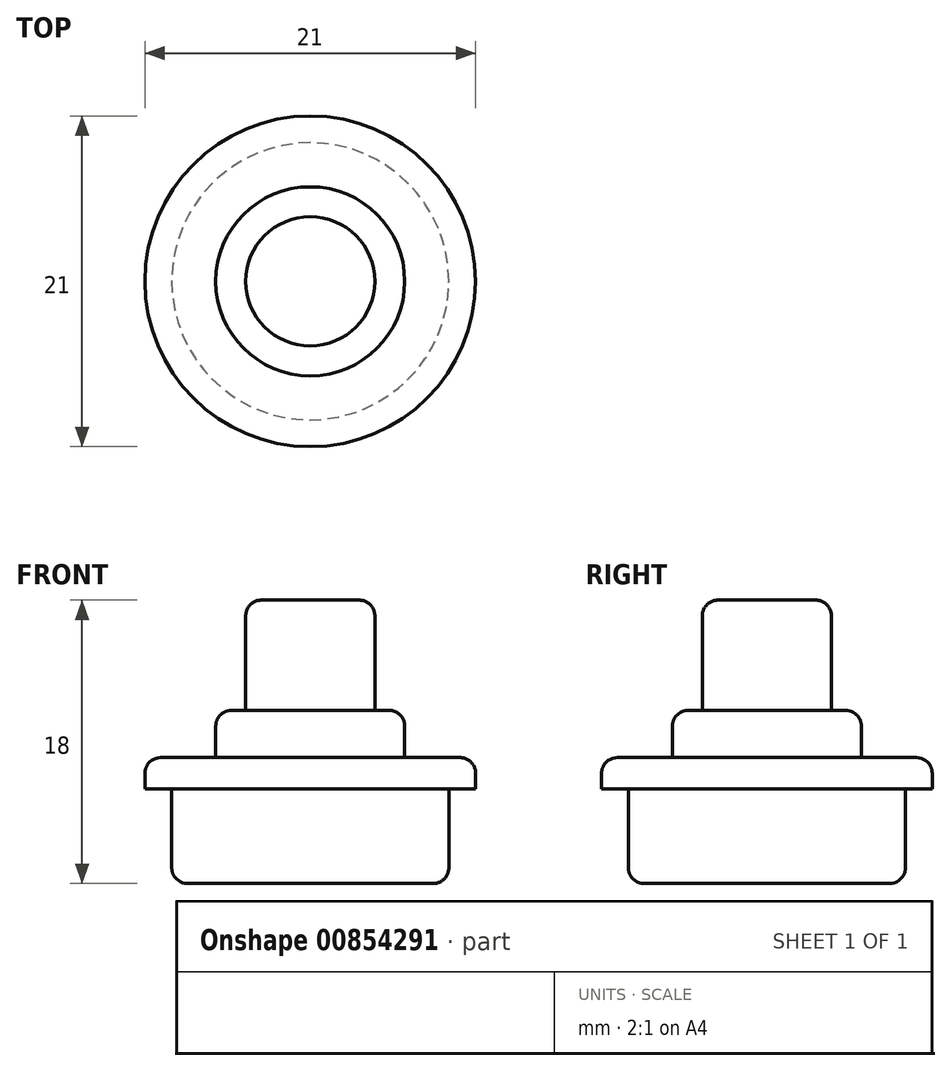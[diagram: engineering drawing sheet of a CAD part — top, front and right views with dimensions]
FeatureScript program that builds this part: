
annotation { "Feature Type Name" : "Feature", "Feature Type Description" : "" }
export const myFeature = defineFeature(function(context is Context, id is Id, definition is map)
    precondition{}
    {
        {
            var Q0;
            Q0=qCreatedBy(makeId("Top.planeOp"),FACE);
            var sketch = newSketch(context, id + "F0", { "sketchPlane" : qUnion([Q0])});
            skCircle(sketch, "E0", {"center": v(0, 0) * mm, "radius": 8.8 * mm});
            skSolve(sketch);
        }
        {
            var Q0;
            Q0=makeQuery(id+"F0.imprint","IMPRINT",FACE,{"disambiguationData":[TD([[makeQuery(id+"F0.imprint","IMPRINT",EDGE,{"derivedFrom":sQuery(id+"F0.wireOp",EDGE,"E0")}),1.0]])]});
            extrude(context, id + "F1", {"entities" : qUnion([Q0]), "depth" : 8 * mm, "offsetDistance" : 25 * mm});
        }
        {
            var Q0;
            Q0=makeQuery(id+"F1.opExtrude","CAP_FACE",FACE,{"disambiguationData":[OSD([sQuery(id+"F0.wireOp",EDGE,"E0")])],"isStart":false});
            var sketch = newSketch(context, id + "F2", { "sketchPlane" : qUnion([Q0])});
            skCircle(sketch, "E1", {"center": v(0, 0) * mm, "radius": 6 * mm});
            skSolve(sketch);
        }
        {
            var Q0;
            Q0=makeQuery(id+"F2.imprint","IMPRINT",FACE,{"disambiguationData":[TD([[makeQuery(id+"F2.imprint","IMPRINT",EDGE,{"derivedFrom":sQuery(id+"F2.wireOp",EDGE,"E1")}),1.0]])]});
            extrude(context, id + "F3", {"entities" : qUnion([Q0]), "operationType" : NewBodyOperationType.ADD, "depth" : 3 * mm, "offsetDistance" : 25 * mm});
        }
        {
            var Q0;
            Q0=makeQuery(id+"F3.opExtrude","CAP_FACE",FACE,{"disambiguationData":[OSD([sQuery(id+"F2.wireOp",EDGE,"E1")])],"isStart":false});
            var sketch = newSketch(context, id + "F4", { "sketchPlane" : qUnion([Q0])});
            skCircle(sketch, "E2", {"center": v(0, 0) * mm, "radius": 4.1 * mm});
            skSolve(sketch);
        }
        {
            var Q0;
            Q0=makeQuery(id+"F4.imprint","IMPRINT",FACE,{"disambiguationData":[TD([[makeQuery(id+"F4.imprint","IMPRINT",EDGE,{"derivedFrom":sQuery(id+"F4.wireOp",EDGE,"E2")}),1.0]])]});
            extrude(context, id + "F5", {"entities" : qUnion([Q0]), "operationType" : NewBodyOperationType.ADD, "depth" : 7 * mm, "offsetDistance" : 25 * mm});
        }
        {
            var Q0;
            Q0=makeQuery(id+"F2.imprint","IMPRINT",FACE,{"disambiguationData":[TD([[makeQuery(id+"F2.imprint","IMPRINT",EDGE,{"derivedFrom":sQuery(id+"F2.wireOp",EDGE,"E1")}),-1.0]])]});
            var sketch = newSketch(context, id + "F6", { "sketchPlane" : qUnion([Q0])});
            skCircle(sketch, "E3", {"center": v(0, 0) * mm, "radius": 10.5 * mm});
            skSolve(sketch);
        }
        {
            var Q0;
            Q0=makeQuery(id+"F6.imprint","IMPRINT",FACE,{"disambiguationData":[TD([[makeQuery(id+"F6.imprint","IMPRINT",EDGE,{"derivedFrom":sQuery(id+"F6.wireOp",EDGE,"E3")}),1.0]])]});
            extrude(context, id + "F7", {"entities" : qUnion([Q0]), "operationType" : NewBodyOperationType.ADD, "oppositeDirection" : true, "depth" : 2 * mm, "offsetDistance" : 25 * mm});
        }
        {
            var Q0;
            Q0=makeQuery(id+"F5.opExtrude","CAP_EDGE",EDGE,{"disambiguationData":[OSD([sQuery(id+"F4.wireOp",EDGE,"E2")])],"isStart":false});
            var Q1;
            Q1=makeQuery(id+"F3.opExtrude","CAP_EDGE",EDGE,{"disambiguationData":[OSD([sQuery(id+"F2.wireOp",EDGE,"E1")])],"isStart":false});
            var Q2;
            Q2=makeQuery(id+"F7.opExtrude","CAP_EDGE",EDGE,{"disambiguationData":[OSD([sQuery(id+"F6.wireOp",EDGE,"E3")])],"isStart":true});
            var Q3;
            Q3=makeQuery(id+"F1.opExtrude","CAP_EDGE",EDGE,{"disambiguationData":[OSD([sQuery(id+"F0.wireOp",EDGE,"E0")])],"isStart":true});
            fillet(context, id + "F8", {"entities" : qUnion([Q0, Q1, Q2, Q3]), "radius" : 1 * mm, "tangentPropagation" : true, "allowEdgeOverflow" : false});
        }
    });
